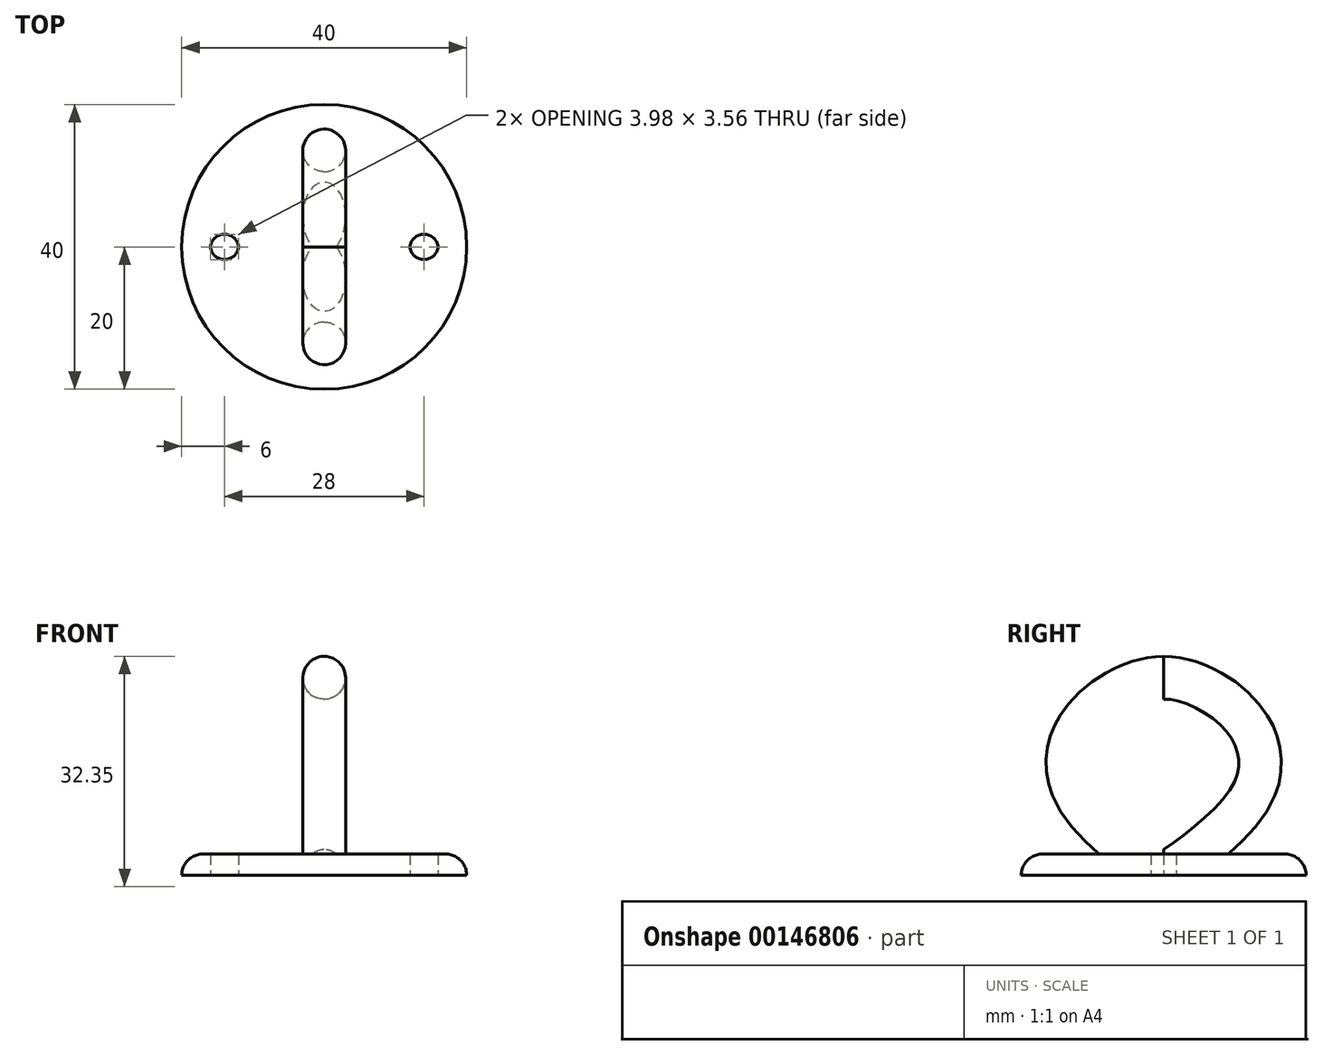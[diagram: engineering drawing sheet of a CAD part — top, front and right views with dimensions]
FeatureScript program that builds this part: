
annotation { "Feature Type Name" : "Feature", "Feature Type Description" : "" }
export const myFeature = defineFeature(function(context is Context, id is Id, definition is map)
    precondition{}
    {
        {
            var Q0;
            Q0=qCreatedBy(makeId("Top.planeOp"),FACE);
            var sketch = newSketch(context, id + "F0", { "sketchPlane" : qUnion([Q0])});
            skCircle(sketch, "E0", {"center": v(0, 0) * mm, "radius": 20 * mm});
            skCircle(sketch, "E1.1.0", {"center": v(-14, -0.22) * mm, "radius": 2 * mm});
            skPoint(sketch, "E1.center", {"position": v(0, -0.22) * mm});
            skCircle(sketch, "E2.1.3.0", {"center": v(14, -0.22) * mm, "radius": 2 * mm});
            skPoint(sketch, "E3.center.orphan", {"position": v(0, 13.78) * mm});
            skSolve(sketch);
        }
        {
            var Q0;
            Q0=makeQuery(id+"F0.imprint","IMPRINT",FACE,{"disambiguationData":[TD([[makeQuery(id+"F0.imprint","IMPRINT",EDGE,{"derivedFrom":sQuery(id+"F0.wireOp",EDGE,"E0")}),1.0]])]});
            extrude(context, id + "F1", {"entities" : qUnion([Q0]), "depth" : 3 * mm});
        }
        {
            var Q0;
            Q0=qCreatedBy(makeId("Right.planeOp"),FACE);
            var sketch = newSketch(context, id + "F2", { "sketchPlane" : qUnion([Q0])});
            skFitSpline(sketch, "E4", {"points": [v(0, 27.73) * mm, v(10.95, 22.3) * mm, v(12.53, 11.64) * mm, v(0, 0) * mm], "startDerivative": vector(33, 0.68) * mm, "endDerivative": vector(-27.06, -17.87) * mm});
            skFitSpline(sketch, "E5.MirrorCS", {"points": [v(0, 27.73) * mm, v(-10.95, 22.3) * mm, v(-12.53, 11.64) * mm, v(0, 0) * mm], "startDerivative": vector(-33, 0.68) * mm, "endDerivative": vector(27.06, -17.87) * mm});
            skSolve(sketch);
        }
        {
            var Q0;
            Q0=qCreatedBy(makeId("Front.planeOp"),FACE);
            var sketch = newSketch(context, id + "F3", { "sketchPlane" : qUnion([Q0])});
            skCircle(sketch, "E6", {"center": v(0, 27.73) * mm, "radius": 3 * mm});
            skSolve(sketch);
        }
        {
            var Q0;
            Q0=makeQuery(id+"F3.imprint","IMPRINT",FACE,{"disambiguationData":[TD([[makeQuery(id+"F3.imprint","IMPRINT",EDGE,{"derivedFrom":sQuery(id+"F3.wireOp",EDGE,"E6")}),1.0]])]});
            var Q1;
            Q1=sQuery(id+"F2.wireOp",EDGE,"E4");
            sweep(context, id + "F4", {"operationType" : NewBodyOperationType.ADD, "profiles" : qUnion([Q0]), "path" : qUnion([Q1])});
        }
        {
            var Q0;
            Q0=qCreatedBy(makeId("Front.planeOp"),FACE);
            var sketch = newSketch(context, id + "F5", { "sketchPlane" : qUnion([Q0])});
            skLineSegment(sketch, "E7.bottom", {"start": v(-16.54, -5.11) * mm, "end": v(19.9, -5.11) * mm});
            skLineSegment(sketch, "E7.top", {"start": v(-16.54, 0) * mm, "end": v(19.9, 0) * mm});
            skLineSegment(sketch, "E7.left", {"start": v(-16.54, -5.11) * mm, "end": v(-16.54, 0) * mm});
            skLineSegment(sketch, "E7.right", {"start": v(19.9, -5.11) * mm, "end": v(19.9, 0) * mm});
            skSolve(sketch);
        }
        {
            var Q0;
            Q0 = qSketchRegion(id + "F5", true);
            extrude(context, id + "F6", {"entities" : qUnion([Q0]), "operationType" : NewBodyOperationType.REMOVE, "oppositeDirection" : true, "depth" : 25 * mm});
        }
        {
            var Q0;
            Q0=makeQuery(id+"F1.opExtrude","SWEPT_BODY",BODY,{"disambiguationData":[OSD([sQuery(id+"F0.wireOp",EDGE,"E0"),sQuery(id+"F0.wireOp",EDGE,"E1.1.0"),sQuery(id+"F0.wireOp",EDGE,"E2.1.3.0")])]});
            var Q1;
            Q1=qCreatedBy(makeId("Front.planeOp"),FACE);
            mirror(context, id + "F7", {"operationType" : NewBodyOperationType.ADD, "entities" : qUnion([Q0]), "mirrorPlane" : qUnion([Q1])});
        }
        {
            var Q0;
            Q0=makeQuery(id+"F1.opExtrude","CAP_EDGE",EDGE,{"disambiguationData":[OSD([sQuery(id+"F0.wireOp",EDGE,"E0")])],"isStart":false});
            fillet(context, id + "F8", {"entities" : qUnion([Q0]), "radius" : 3 * mm, "tangentPropagation" : true, "allowEdgeOverflow" : false});
        }
    });
